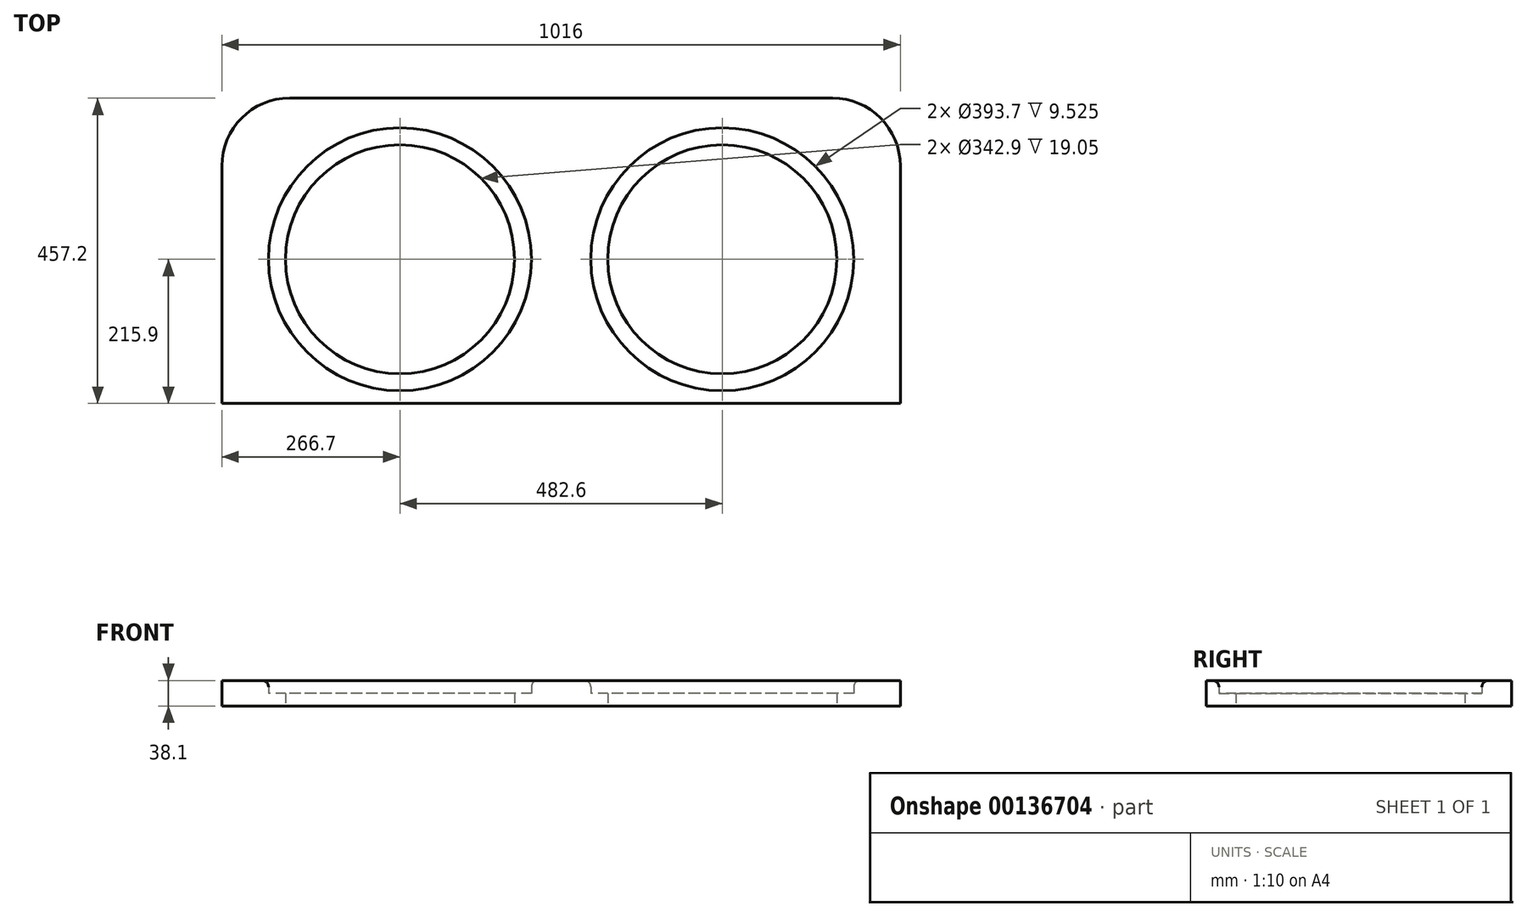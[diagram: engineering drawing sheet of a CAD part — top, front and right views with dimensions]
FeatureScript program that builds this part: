
annotation { "Feature Type Name" : "Feature", "Feature Type Description" : "" }
export const myFeature = defineFeature(function(context is Context, id is Id, definition is map)
    precondition{}
    {
        {
            var Q0;
            Q0=qCreatedBy(makeId("Top.planeOp"),FACE);
            var sketch = newSketch(context, id + "F0", { "sketchPlane" : qUnion([Q0])});
            skLineSegment(sketch, "E0.bottom", {"start": v(0, 0) * mm, "end": v(1016, 0) * mm});
            skLineSegment(sketch, "E0.top", {"start": v(101.6, 457.2) * mm, "end": v(914.4, 457.2) * mm});
            skLineSegment(sketch, "E0.left", {"start": v(0, 0) * mm, "end": v(0, 355.6) * mm});
            skLineSegment(sketch, "E0.right", {"start": v(1016, 0) * mm, "end": v(1016, 355.6) * mm});
            skArc(sketch, "E1", {"start": v(101.6, 457.2) * mm, "mid": v(29.76, 427.44) * mm, "end": v(0, 355.6) * mm});
            skArc(sketch, "E2", {"start": v(1016, 355.6) * mm, "mid": v(986.24, 427.44) * mm, "end": v(914.4, 457.2) * mm});
            skCircle(sketch, "E3", {"center": v(266.7, 215.9) * mm, "radius": 196.85 * mm});
            skCircle(sketch, "E4", {"center": v(749.3, 215.9) * mm, "radius": 196.85 * mm});
            skCircle(sketch, "E5", {"center": v(749.3, 215.9) * mm, "radius": 171.45 * mm});
            skCircle(sketch, "E6", {"center": v(266.7, 215.9) * mm, "radius": 171.45 * mm});
            skSolve(sketch);
        }
        {
            var Q0;
            Q0=makeQuery(id+"F0.imprint","IMPRINT",FACE,{"disambiguationData":[TD([[makeQuery(id+"F0.imprint","IMPRINT",EDGE,{"derivedFrom":sQuery(id+"F0.wireOp",EDGE,"E0.bottom")}),1.0]])]});
            extrude(context, id + "F1", {"entities" : qUnion([Q0]), "depth" : 38.1 * mm});
        }
        {
            var Q0;
            Q0=makeQuery(id+"F0.imprint","IMPRINT",FACE,{"disambiguationData":[TD([[makeQuery(id+"F0.imprint","IMPRINT",EDGE,{"derivedFrom":sQuery(id+"F0.wireOp",EDGE,"E3")}),1.0]])]});
            var Q1;
            Q1=makeQuery(id+"F0.imprint","IMPRINT",FACE,{"disambiguationData":[TD([[makeQuery(id+"F0.imprint","IMPRINT",EDGE,{"derivedFrom":sQuery(id+"F0.wireOp",EDGE,"E4")}),1.0]])]});
            extrude(context, id + "F2", {"entities" : qUnion([Q0, Q1]), "operationType" : NewBodyOperationType.ADD, "depth" : 19.05 * mm});
        }
        {
            var Q0;
            Q0=makeQuery(id+"F1.opExtrude","CAP_EDGE",EDGE,{"disambiguationData":[OSD([sQuery(id+"F0.wireOp",EDGE,"E3")])],"isStart":false});
            var Q1;
            Q1=makeQuery(id+"F1.opExtrude","CAP_EDGE",EDGE,{"disambiguationData":[OSD([sQuery(id+"F0.wireOp",EDGE,"E4")])],"isStart":false});
            fillet(context, id + "F3", {"entities" : qUnion([Q0, Q1]), "radius" : 9.52 * mm, "tangentPropagation" : true, "allowEdgeOverflow" : false});
        }
    });
